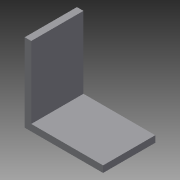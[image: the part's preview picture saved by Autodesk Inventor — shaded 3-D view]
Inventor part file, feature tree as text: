
AUTODESK INVENTOR PART (.ipt)
format: ipt  version: 2015 (Build 190159000, 159)  size: 73,728 bytes
history: native  units: in
note: dims shown in document units (in); Inventor stores cm internally (conversion verified against a paired STEP export)
features: other x3, sketch x2
ambient origin geometry x8: Origin, YZ Plane, XZ Plane, XY Plane, X Axis, Y Axis, Z Axis, Center Point
bodies: Solid1 (feature_tree)
feature tree (5):
  other  "14in L Mount.ipt"
  other  "Solid1::14in L Mount.ipt"
  other  "TaggingFeature1"
  sketch  "Sketch1"  dims[d0=0.3937in]
  sketch  "Sketch2"
